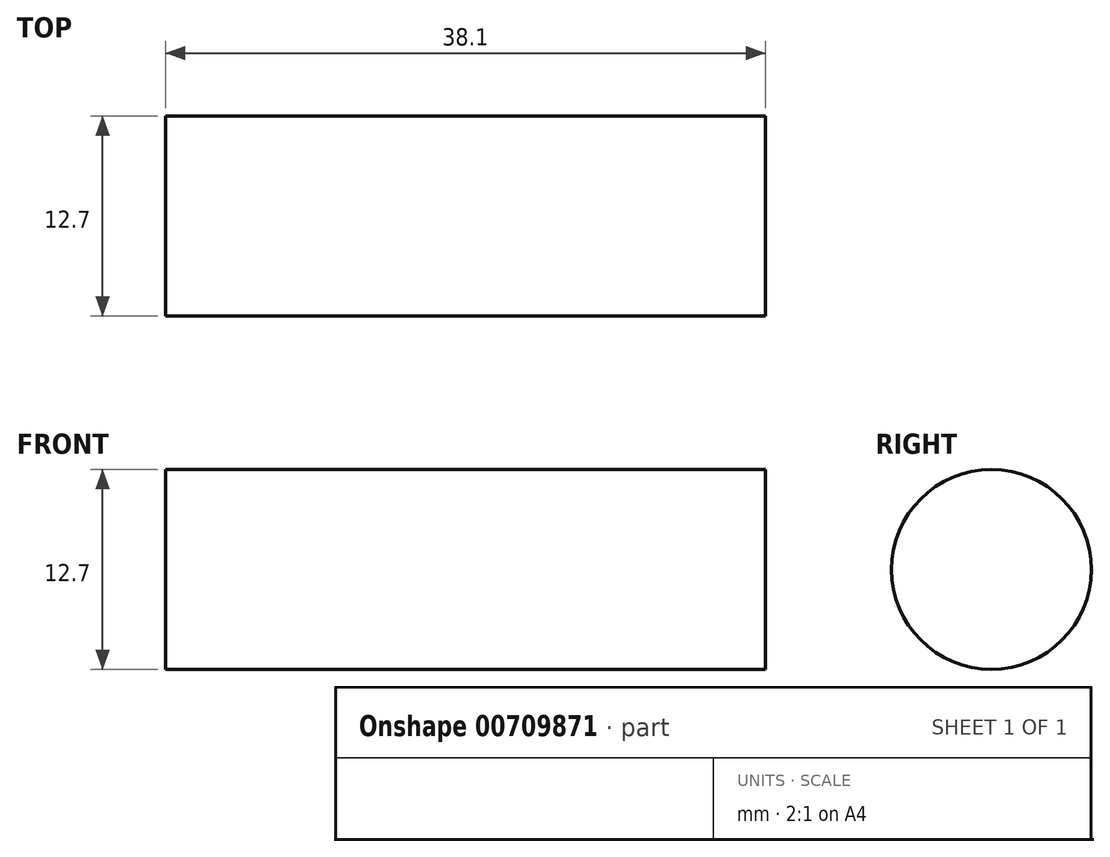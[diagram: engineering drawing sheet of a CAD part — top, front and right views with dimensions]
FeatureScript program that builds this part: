
annotation { "Feature Type Name" : "Feature", "Feature Type Description" : "" }
export const myFeature = defineFeature(function(context is Context, id is Id, definition is map)
    precondition{}
    {
        {
            var Q0;
            Q0=qCreatedBy(makeId("Right.planeOp"),FACE);
            var sketch = newSketch(context, id + "F0", { "sketchPlane" : qUnion([Q0])});
            skCircle(sketch, "E0", {"center": v(0, 0) * mm, "radius": 6.35 * mm});
            skSolve(sketch);
        }
        {
            var Q0;
            Q0 = qSketchRegion(id + "F0", true);
            extrude(context, id + "F1", {"entities" : qUnion([Q0]), "endBound" : BoundingType.SYMMETRIC, "depth" : 38.1 * mm, "offsetDistance" : 25.4 * mm});
        }
    });
